# Revit family: Wall_Ceiling-Panel-Armstrong-Tectum-Sq-Direct-Attach-8180
name_source: partatom
category: Specialty Equipment
revit_build: Autodesk Revit MEP 2012 (Build: 20110916_2132(x64)
units: mm (PartAtom-declared; Revit-internal decimal feet)

## types (1)
- Direct-Attach-Wall and Ceiling panel_Tectum
    04 CSI = 09 84 00
    10 Yr Availability = No
    95 CSI = 09800
    Assembly Code = C3030220
    BTU Insulation Value = 0 Btu
    Ceililing Recycle Prgm = No
    Cert  Low Voc Emissions = Yes
    Color Code = Included With Color Name
    Color Finish = White TWH; Natural TNA
    Default Elevation = 4' - 0"
    Description = Ceiling/Wall Panel
    Downward Accessible = No
    Fire Performance = Class A
    Humidity Resistance = Humiguard Plus
    Impact Resistant = Yes
    Light Reflectance = 0.86
    Manufacturer = Armstrong Ceilings
    Manufacturer Fax = 1 800-572-TECH
    Material = Cementitious Wood Fiber
    Material Process = Not Published
    Model = 8180
    Mold Mildew Resistance = BioBlock
    NRC = d
    Panel = Tectum - Direct Attach Ceiling Panel - 8180 - Natural
    Pcs Pallet = 72 PCS/PALLET
    Product Page URL = https://www.armstrongceilings.com
    Recycle Content = Not Published
    Revit Object Download Link = http://library.smartbim.com
    Scratch Resistant = Yes
    Scrubbable = Yes
    Seismic Tested = Yes
    Soil Resistant = Yes
    Surface Finish = Factory-applied latex paint with Silicate surface coating
    Sustain = Yes
    Texture = Coarse
    Thickness = 0' - 1"
    URL = http://www.armstrongceilings.com
    Washable = Yes
    Watts Insulation Value = 0 W
    Wt Per Item = 0.90 lb

## geometry (parser evidence)
native form markers: Blend x1, Sweep x1
no freeform markers — native parametric forms only
